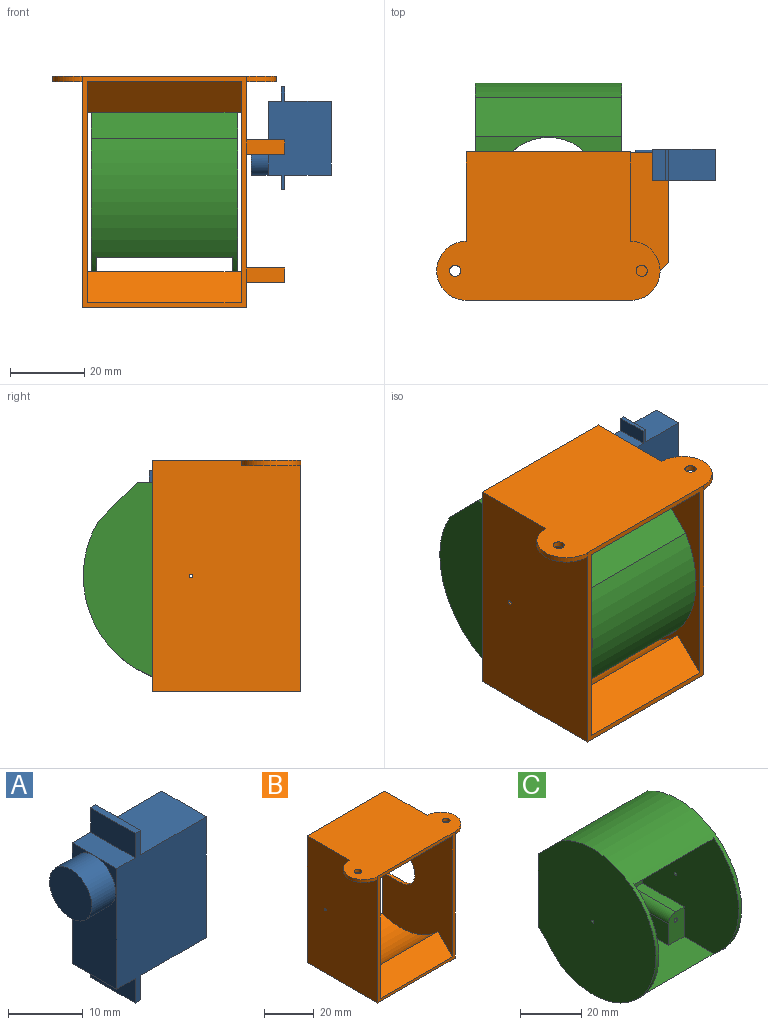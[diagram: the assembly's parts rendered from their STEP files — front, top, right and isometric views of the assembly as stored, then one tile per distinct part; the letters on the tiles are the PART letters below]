
ASSEMBLY  parts=3 mates=1
PART A: 16 faces, bbox 21.5x8.5x27.8 mm
  f0: plane 8.46x3.5mm, normal (0,0,1), area 29.6mm2, adj f2,f4,f7,f15
  f1: plane 8.46x3.5mm, normal (0,0,-1), area 29.6mm2, adj f2,f4,f7,f12
  f2: plane 27.8x17mm, normal (0,-1,0), area 344.6mm2, adj f0,f1,f3,f5,f6,f7,f10,f11
  f3: plane 12.5x8.46mm, normal (0,0,-1), area 105.7mm2, adj f2,f4,f6,f11
  f4: plane 27.8x17mm, normal (0,1,0), area 344.6mm2, adj f0,f1,f3,f5,f6,f7,f10,f11
  f5: plane 12.5x8.46mm, normal (0,0,1), area 105.8mm2, adj f2,f4,f6,f14
  f6: plane 19.8x8.46mm, normal (1,0,0), area 167.5mm2, adj f2,f3,f4,f5
  f7: plane 19.8x8.46mm, normal (-1,0,0), area 117.2mm2, adj f0,f1,f2,f4,f8
  f8: cylinder r=4mm len=8mm, axis (1,0,0), area 113.1mm2, adj f7,f9
  f9: plane 8x8mm, normal (-1,0,0), area 50.3mm2, adj f8
  f10: plane 8.46x1mm, normal (0,0,-1), area 8.5mm2, adj f2,f4,f11,f12
  f11: plane 8.46x4mm, normal (1,0,0), area 33.8mm2, adj f2,f3,f4,f10
  f12: plane 8.46x4mm, normal (-1,0,0), area 33.8mm2, adj f1,f2,f4,f10
  f13: plane 8.46x1mm, normal (0,0,1), area 8.5mm2, adj f2,f4,f14,f15
  f14: plane 8.46x4mm, normal (1,0,0), area 33.8mm2, adj f2,f4,f5,f13
  f15: plane 8.46x4mm, normal (-1,0,0), area 33.8mm2, adj f0,f2,f4,f13
PART B: 36 faces, bbox 62.4x39.9x62.4 mm
  f0: plane 62.4x54.5mm, normal (0,1,0), area 477.2mm2, adj f1,f3,f4,f5,f6,f7,f8,f9
  f1: plane 60.4x39.94mm, normal (1,0,0), area 2108.5mm2, adj f0,f11,f16,f17,f18,f19,f30,f31
  f2: cylinder r=0.5mm len=1mm, axis (1,0,0), area 3.1mm2, adj f15,f33
  f3: plane 29.64x4mm, normal (1,0,0), area 118.5mm2, adj f0,f4,f5,f29
  f4: plane 39.94x10.3mm, normal (0,0,1), area 358.3mm2, adj f0,f3,f10,f29
  f5: plane 39.94x10.3mm, normal (0,0,-1), area 358.3mm2, adj f0,f3,f9,f29
  f6: plane 29.64x4mm, normal (1,0,0), area 118.5mm2, adj f0,f7,f8,f28
  f7: plane 39.94x10.3mm, normal (0,0,1), area 358.3mm2, adj f0,f6,f9,f28
  f8: plane 39.94x10.3mm, normal (0,0,-1), area 358.3mm2, adj f0,f6,f14,f28
  f9: plane 39.94x30.48mm, normal (1,0,0), area 945.1mm2, adj f0,f5,f7,f11,f21,f22,f23
  f10: plane 39.94x17.17mm, normal (1,0,0), area 661.7mm2, adj f0,f4,f11,f12,f25,f35
  f11: plane 62.4x44.2mm, normal (0,-1,0), area 303.2mm2, adj f1,f9,f10,f12,f13,f14,f15,f17
  f12: plane 60.1x39.94mm, normal (0,0,1), area 1949.6mm2, adj f0,f10,f11,f15,f24,f26,f34,f35
  f13: plane 44.2x39.94mm, normal (0,0,-1), area 1765.1mm2, adj f0,f11,f14,f15
  f14: plane 39.94x6.75mm, normal (1,0,0), area 269.7mm2, adj f0,f8,f11,f13
  f15: plane 62.4x39.94mm, normal (-1,0,0), area 2467.3mm2, adj f0,f2,f11,f12,f13,f27,f34
  f16: cylinder r=30.2mm len=41.2mm, axis (1,0,0), area 1407.7mm2, adj f0,f1,f17,f20
  f17: plane 41.2x8.29mm, normal (0,-0.71,-0.71), area 483.1mm2, adj f1,f11,f16,f20
  f18: plane 41.2x8.29mm, normal (0,-0.71,0.71), area 483.1mm2, adj f1,f11,f19,f20
  f19: cylinder r=30.2mm len=41.2mm, axis (1,0,0), area 1407.7mm2, adj f0,f1,f18,f20
  f20: plane 60.4x39.94mm, normal (-1,0,0), area 1936.8mm2, adj f0,f11,f16,f17,f18,f19,f21,f22
  f21: plane 10.44x1.5mm, normal (0,0,-1), area 15.7mm2, adj f0,f9,f20,f22
  f22: cylinder r=8.1mm len=16.2mm, axis (1,0,0), area 38.2mm2, adj f9,f20,f21,f23
  f23: plane 10.44x1.5mm, normal (0,0,1), area 15.7mm2, adj f0,f9,f20,f22
  f24: cylinder r=1.5mm len=3mm, axis (0,0,1), area 14.1mm2, adj f12,f25
  f25: plane 15.9x7.95mm, normal (0,0,-1), area 92.2mm2, adj f10,f24,f35
  f26: cylinder r=1.5mm len=3mm, axis (0,0,1), area 14.1mm2, adj f12,f27
  f27: plane 15.9x7.95mm, normal (0,0,-1), area 92.2mm2, adj f15,f26,f34
  f28: plane 10.3x10.3mm, normal (0.71,-0.71,0), area 58.3mm2, adj f6,f7,f8,f11
  f29: plane 10.3x10.3mm, normal (0.71,-0.71,0), area 58.3mm2, adj f3,f4,f5,f11
  f30: plane 10.44x0.5mm, normal (0,0,-1), area 5.2mm2, adj f0,f1,f31,f33
  f31: cylinder r=3.75mm len=7.5mm, axis (1,0,0), area 5.9mm2, adj f1,f30,f32,f33
  f32: plane 10.44x0.5mm, normal (0,0,1), area 5.2mm2, adj f0,f1,f31,f33
  f33: plane 14.19x7.5mm, normal (1,0,0), area 99.6mm2, adj f0,f2,f30,f31,f32
  f34: cylinder r=7.95mm len=15.9mm, axis (0,0,1), area 37.5mm2, adj f11,f12,f15,f27
  f35: cylinder r=7.95mm len=15.9mm, axis (0,0,1), area 37.5mm2, adj f10,f11,f12,f25
PART C: 40 faces, bbox 39.5x54.1x58 mm
  f0: plane 11.75x7.13mm, normal (0,-1,0), area 79.7mm2, adj f10,f13,f18,f19,f20,f33
  f1: plane 11.75x7.13mm, normal (0,-1,0), area 79.7mm2, adj f10,f11,f15,f16,f17,f31
  f2: plane 11.75x7.13mm, normal (0,-1,0), area 79.7mm2, adj f12,f13,f21,f22,f23,f27
  f3: plane 11.75x7.13mm, normal (0,-1,0), area 79.7mm2, adj f11,f12,f24,f25,f26,f29
  f4: plane 39.5x29mm, normal (0,1,0), area 496.3mm2, adj f5,f7,f8,f9,f39
  f5: plane 39.5x10.61mm, normal (0,0.71,0.71), area 593mm2, adj f4,f6,f8,f9
  f6: cylinder r=29mm len=58mm, axis (-1,0,0), area 2846mm2, adj f5,f7,f8,f9,f10,f11,f12,f13
  f7: plane 39.5x10.61mm, normal (0,0.71,-0.71), area 593mm2, adj f4,f6,f8,f9
  f8: plane 58x54.11mm, normal (1,0,0), area 2545.3mm2, adj f4,f5,f6,f7,f38
  f9: plane 58x54.11mm, normal (-1,0,0), area 2545.3mm2, adj f4,f5,f6,f7,f37
  f10: plane 46x44.11mm, normal (-1,0,0), area 1424.5mm2, adj f0,f1,f6,f11,f13,f14,f17,f18
  f11: plane 36.75x32.78mm, normal (0,0,1), area 933.9mm2, adj f1,f3,f6,f10,f12,f14,f15,f26
  f12: plane 46x44.11mm, normal (1,0,0), area 1424.5mm2, adj f2,f3,f6,f11,f13,f14,f23,f24
  f13: plane 36.75x32.78mm, normal (0,0,-1), area 933.9mm2, adj f0,f2,f6,f10,f12,f14,f20,f21
  f14: plane 46x36.75mm, normal (0,-1,0), area 609.9mm2, adj f10,f11,f12,f13,f15,f16,f17,f18
  f15: plane 19x8.5mm, normal (-1,0,0), area 161.5mm2, adj f1,f11,f14,f16
  f16: cylinder r=3.25mm len=19mm, axis (0,-1,0), area 97mm2, adj f1,f14,f15,f17
  f17: plane 19x3.88mm, normal (0,0,1), area 73.6mm2, adj f1,f10,f14,f16
  f18: plane 19x3.88mm, normal (0,0,-1), area 73.6mm2, adj f0,f10,f14,f19
  f19: cylinder r=3.25mm len=19mm, axis (0,-1,0), area 97mm2, adj f0,f14,f18,f20
  f20: plane 19x8.5mm, normal (-1,0,0), area 161.5mm2, adj f0,f13,f14,f19
  f21: plane 19x8.5mm, normal (1,0,0), area 161.5mm2, adj f2,f13,f14,f22
  f22: cylinder r=3.25mm len=19mm, axis (0,-1,0), area 97mm2, adj f2,f14,f21,f23
  f23: plane 19x3.88mm, normal (0,0,-1), area 73.6mm2, adj f2,f12,f14,f22
  f24: plane 19x3.88mm, normal (0,0,1), area 73.6mm2, adj f3,f12,f14,f25
  f25: cylinder r=3.25mm len=19mm, axis (0,-1,0), area 97mm2, adj f3,f14,f24,f26
  f26: plane 19x8.5mm, normal (1,0,0), area 161.5mm2, adj f3,f11,f14,f25
  f27: cylinder r=0.75mm len=19mm, axis (0,-1,0), area 89.5mm2, adj f2,f28
  f28: plane 1.5x1.5mm, normal (0,-1,0), area 1.8mm2, adj f27
  f29: cylinder r=0.75mm len=19mm, axis (0,-1,0), area 89.5mm2, adj f3,f30
  f30: plane 1.5x1.5mm, normal (0,-1,0), area 1.8mm2, adj f29
  f31: cylinder r=0.75mm len=19mm, axis (0,-1,0), area 89.5mm2, adj f1,f32
  f32: plane 1.5x1.5mm, normal (0,-1,0), area 1.8mm2, adj f31
  f33: cylinder r=0.75mm len=19mm, axis (0,-1,0), area 89.5mm2, adj f0,f34
  f34: plane 1.5x1.5mm, normal (0,-1,0), area 1.8mm2, adj f33
  f35: plane 31x31mm, normal (0,-1,0), area 105.6mm2, adj f36,f39
  f36: cylinder r=15.5mm len=31mm, axis (0,-1,0), area 584.3mm2, adj f14,f35
  f37: cylinder r=0.5mm len=1.38mm, axis (1,0,0), area 4.3mm2, adj f9,f12
  f38: cylinder r=0.5mm len=1.38mm, axis (1,0,0), area 4.3mm2, adj f8,f10
  f39: cylinder r=14.38mm len=28.75mm, axis (0,-1,0), area 361.3mm2, adj f4,f35
PLACE A rot(axis=(1,0,0),180deg) t=(11.5,9.49,10.77)mm
PLACE B rot(axis=(1,0,0),0deg) t=(11.02,2.49,2.22)mm
PLACE C rot(axis=(1,0,0),90deg) t=(11.37,2.49,2.22)mm
MATE revolute B.f2 <-> C.f6  axis (1,0,0) through (11.37,2.49,2.22)mm
